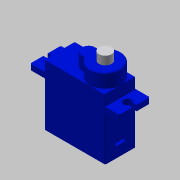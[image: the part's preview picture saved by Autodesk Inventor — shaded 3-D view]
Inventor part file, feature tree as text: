
AUTODESK INVENTOR PART (.ipt)
format: ipt  version: 2019.2 (Build 232265000, 265)  size: 240,640 bytes
history: native  units: mm
features: extrude x5, sketch x5, other x2, fillet x1
ambient origin geometry x8: Origin, YZ Plane, XZ Plane, XY Plane, X Axis, Y Axis, Z Axis, Center Point
bodies: Body1 (feature_tree)
feature tree (13):
  other  "솔리드1"
  extrude  "돌출1"  Depth=22.0mm
  other  "작업 평면1"
  extrude  "돌출2"  Depth=11.0mm
  extrude  "돌출3"  Depth=22.0mm TaperAngle=0.0deg
  fillet  "모깎기1"  [1 undecoded]
  extrude  "돌출4"  Depth=5.0mm
  extrude  "돌출6"  Depth=5.0mm
  sketch  "스케치1"
  sketch  "스케치2"
  sketch  "스케치3"
  sketch  "스케치4"
  sketch  "스케치6"
note: 1 required parameter value undecoded (feature->parameter linkage not recoverable at this tier; creation-order binding heuristic only, values carry confidence <= 0.55)
